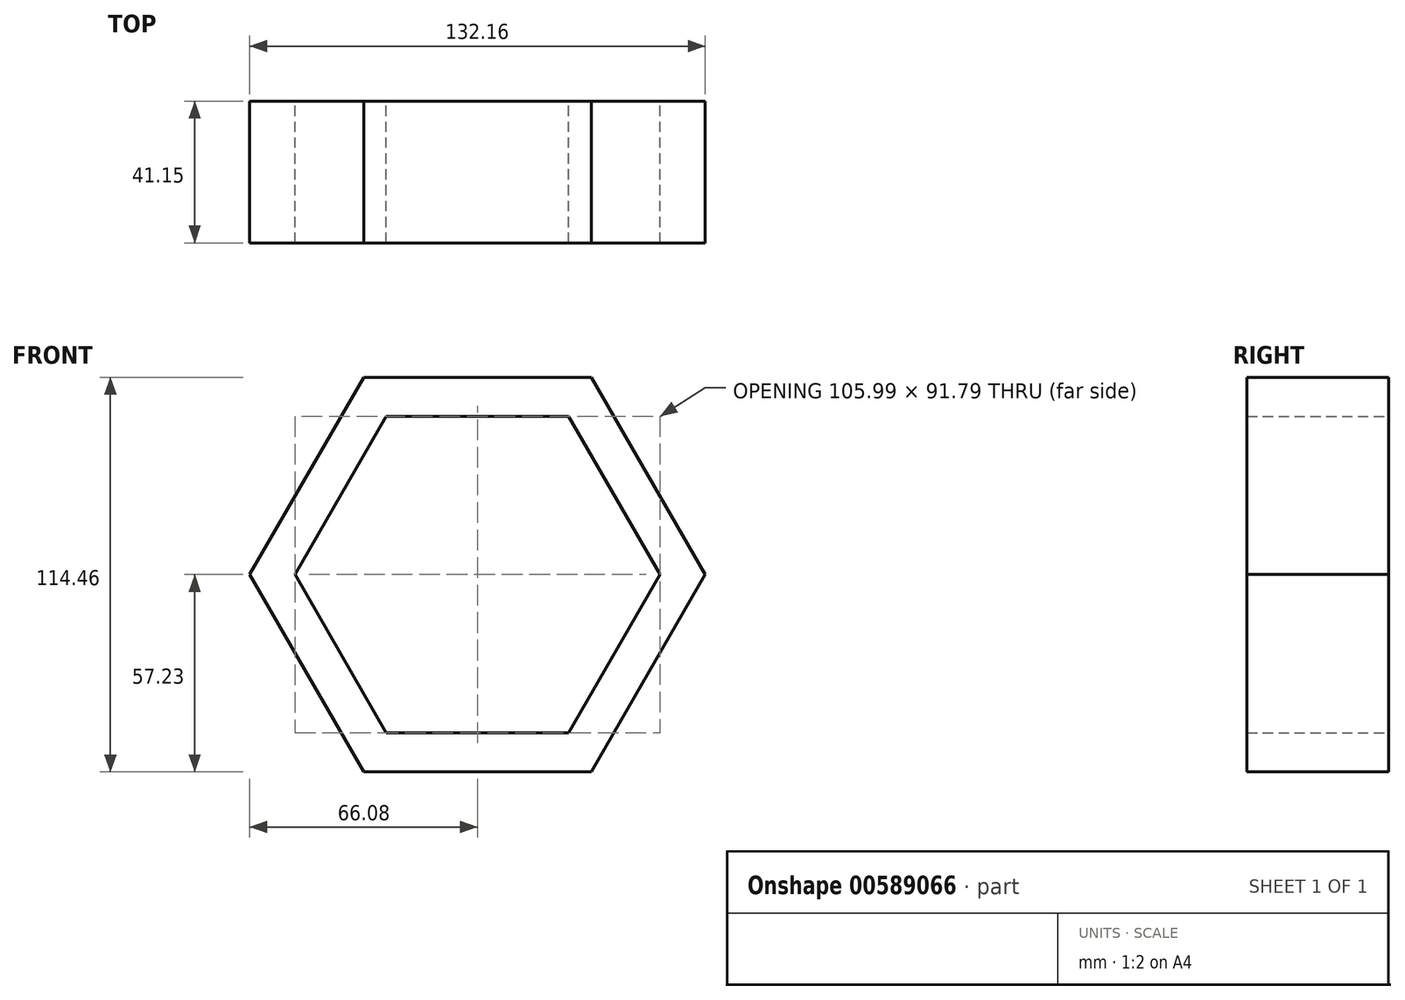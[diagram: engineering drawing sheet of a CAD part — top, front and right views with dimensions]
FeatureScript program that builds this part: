
annotation { "Feature Type Name" : "Feature", "Feature Type Description" : "" }
export const myFeature = defineFeature(function(context is Context, id is Id, definition is map)
    precondition{}
    {
        {
            var Q0;
            Q0=qCreatedBy(makeId("Front.planeOp"),FACE);
            var sketch = newSketch(context, id + "F0", { "sketchPlane" : qUnion([Q0])});
            skCircle(sketch, "E0.cCircle", {"center": v(0, 0) * mm, "radius": 57.23 * mm, "construction": true});
            skLineSegment(sketch, "E0.0", {"start": v(-33.04, 57.23) * mm, "end": v(33.04, 57.23) * mm});
            skLineSegment(sketch, "E0.1", {"start": v(33.04, 57.23) * mm, "end": v(66.08, 0) * mm});
            skLineSegment(sketch, "E0.2", {"start": v(66.08, 0) * mm, "end": v(33.04, -57.23) * mm});
            skLineSegment(sketch, "E0.3", {"start": v(33.04, -57.23) * mm, "end": v(-33.04, -57.23) * mm});
            skLineSegment(sketch, "E0.4", {"start": v(-33.04, -57.23) * mm, "end": v(-66.08, 0) * mm});
            skLineSegment(sketch, "E0.5", {"start": v(-66.08, 0) * mm, "end": v(-33.04, 57.23) * mm});
            skPoint(sketch, "E0.0.midPoint", {"position": v(0, 57.23) * mm});
            skSolve(sketch);
        }
        {
            var Q0;
            Q0=makeQuery(id+"F0.imprint","IMPRINT",FACE,{"disambiguationData":[TD([[makeQuery(id+"F0.imprint","IMPRINT",EDGE,{"derivedFrom":sQuery(id+"F0.wireOp",EDGE,"E0.0")}),-1.0]])]});
            extrude(context, id + "F1", {"entities" : qUnion([Q0]), "depth" : 41.15 * mm, "offsetDistance" : 25.4 * mm});
        }
        {
            var Q0;
            Q0=makeQuery(id+"F1.opExtrude","CAP_FACE",FACE,{"disambiguationData":[OSD([sQuery(id+"F0.wireOp",EDGE,"E0.0"),sQuery(id+"F0.wireOp",EDGE,"E0.1"),sQuery(id+"F0.wireOp",EDGE,"E0.2"),sQuery(id+"F0.wireOp",EDGE,"E0.3"),sQuery(id+"F0.wireOp",EDGE,"E0.4"),sQuery(id+"F0.wireOp",EDGE,"E0.5")])],"isStart":true});
            var sketch = newSketch(context, id + "F2", { "sketchPlane" : qUnion([Q0])});
            skCircle(sketch, "E1.cCircle", {"center": v(0, 0) * mm, "radius": 45.9 * mm, "construction": true});
            skLineSegment(sketch, "E1.0", {"start": v(-26.5, 45.9) * mm, "end": v(26.5, 45.9) * mm});
            skLineSegment(sketch, "E1.1", {"start": v(26.5, 45.9) * mm, "end": v(53, 0) * mm});
            skLineSegment(sketch, "E1.2", {"start": v(53, 0) * mm, "end": v(26.5, -45.9) * mm});
            skLineSegment(sketch, "E1.3", {"start": v(26.5, -45.9) * mm, "end": v(-26.5, -45.9) * mm});
            skLineSegment(sketch, "E1.4", {"start": v(-26.5, -45.9) * mm, "end": v(-53, 0) * mm});
            skLineSegment(sketch, "E1.5", {"start": v(-53, 0) * mm, "end": v(-26.5, 45.9) * mm});
            skPoint(sketch, "E1.0.midPoint", {"position": v(0, 45.9) * mm});
            skSolve(sketch);
        }
        {
            var Q0;
            Q0=makeQuery(id+"F2.imprint","IMPRINT",FACE,{"disambiguationData":[TD([[makeQuery(id+"F2.imprint","IMPRINT",EDGE,{"derivedFrom":sQuery(id+"F2.wireOp",EDGE,"E1.0")}),-1.0]])]});
            extrude(context, id + "F3", {"entities" : qUnion([Q0]), "operationType" : NewBodyOperationType.REMOVE, "oppositeDirection" : true, "depth" : 166.88 * mm, "offsetDistance" : 25.4 * mm});
        }
        {
            var Q0;
            Q0=makeQuery(id+"F1.opExtrude","CAP_FACE",FACE,{"disambiguationData":[OSD([sQuery(id+"F0.wireOp",EDGE,"E0.0"),sQuery(id+"F0.wireOp",EDGE,"E0.1"),sQuery(id+"F0.wireOp",EDGE,"E0.2"),sQuery(id+"F0.wireOp",EDGE,"E0.3"),sQuery(id+"F0.wireOp",EDGE,"E0.4"),sQuery(id+"F0.wireOp",EDGE,"E0.5")])],"isStart":false});
            var sketch = newSketch(context, id + "F4", { "sketchPlane" : qUnion([Q0])});
            skLineSegment(sketch, "E2", {"start": v(0, 57.23) * mm, "end": v(0, -57.23) * mm});
            skSolve(sketch);
        }
    });
